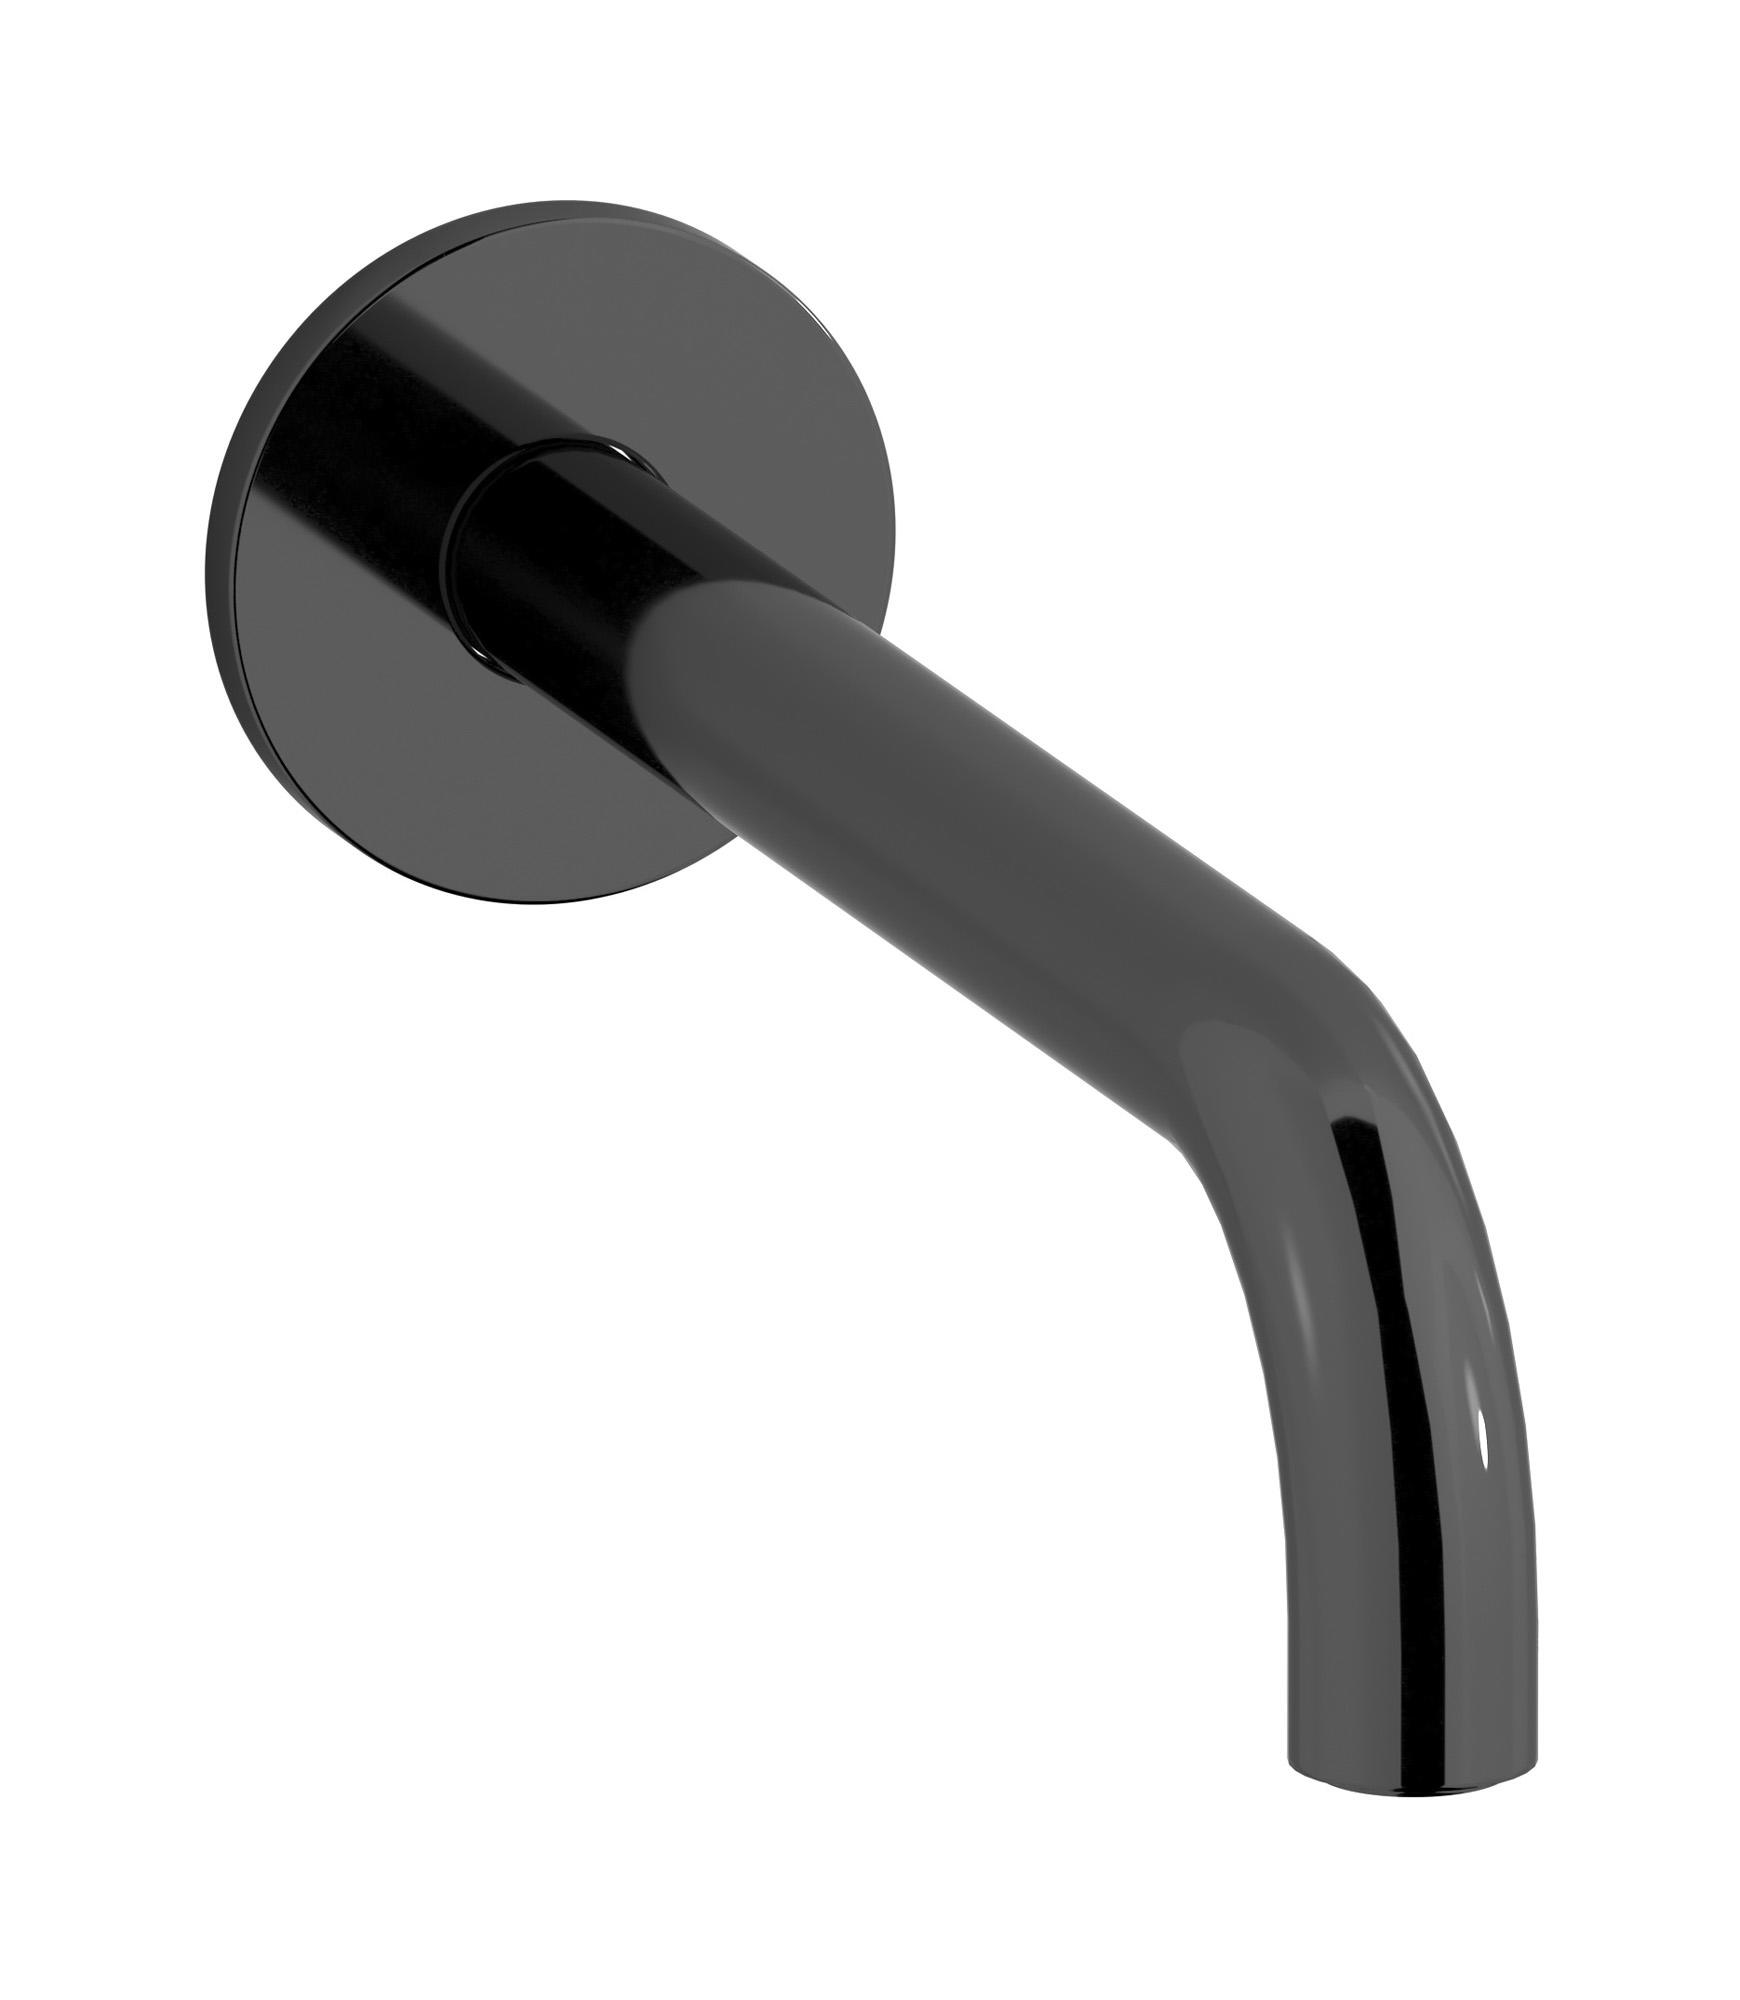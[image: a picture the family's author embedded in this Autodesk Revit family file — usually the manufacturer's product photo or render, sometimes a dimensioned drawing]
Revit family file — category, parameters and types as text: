
# Revit family: RX320
name_source: partatom
category: Apparecchi idraulici
units: mm (PartAtom-declared; Revit-internal decimal feet)

## family parameters
Basato su piano di lavoro = No
Condiviso = No
Mantieni orientamento annotazione = No
Numero OmniClass = 23.45.55.17
Punto di calcolo locali = No
Quota connettore circolare = Usa diametro
Sempre verticale = Sì
Taglio con vuoti quando caricato = No
Tipo di parte = Normale
Titolo OmniClass = Mixing Faucets

## types (12) — shared parameters
Commenti sul tipo = Wall mounted spout
Connessione CW = No
Connessione HW = No
Connessione di scarico = No
Connessione di ventilazione = No
Descrizione = Wall mounted spout
Produttore = IB Rubinetterie S.p.A.
URL = https://www.weareib.it
Water inlet = 10 mm  [stored 0.0328084 ft]
zero-valued in all types: Prospetto di default

## per-type parameters (varying)
| type | Finishes surface | Immagine tipo | Modello |
| Chrome | IB_Chrome | RX320CC.jpg | RX320CC |
| Black Chrome | IB_Black chrome | RX320CF.jpg | RX320CF |
| Brushed Black Chrome | IB_Brushed black chrome | RX320CS.jpg | RX320CS |
| Pale Gold | IB_Pale gold | RX320II.jpg | RX320II |
| Brushed Pale Gold | IB_brushed pale gold | RX320IS.jpg | RX320IS |
| Matt Black | IB_matt black | RX320NP.jpg | RX320NP |
| Natural Brass | IB_Brass | RX320ON.jpg | RX320ON |
| Gold | IB_gold | RX320OO.jpg | RX320OO |
| Brushed Gold | IB_brushed gold | RX320OS.jpg | RX320OS |
| Rose Gold | IB_Rose gold | RX320RS.jpg | RX320RS |
| Brushed Rose Gold | IB_Brushed rose gold | RX320SR.jpg | RX320SR |
| Brushed Nickel | IB_Brushed nickel | RX320SS.jpg | RX320SS |

note: [stored X ft] marks values corroborated as IEEE doubles in the binary element streams (Revit-internal decimal feet)
